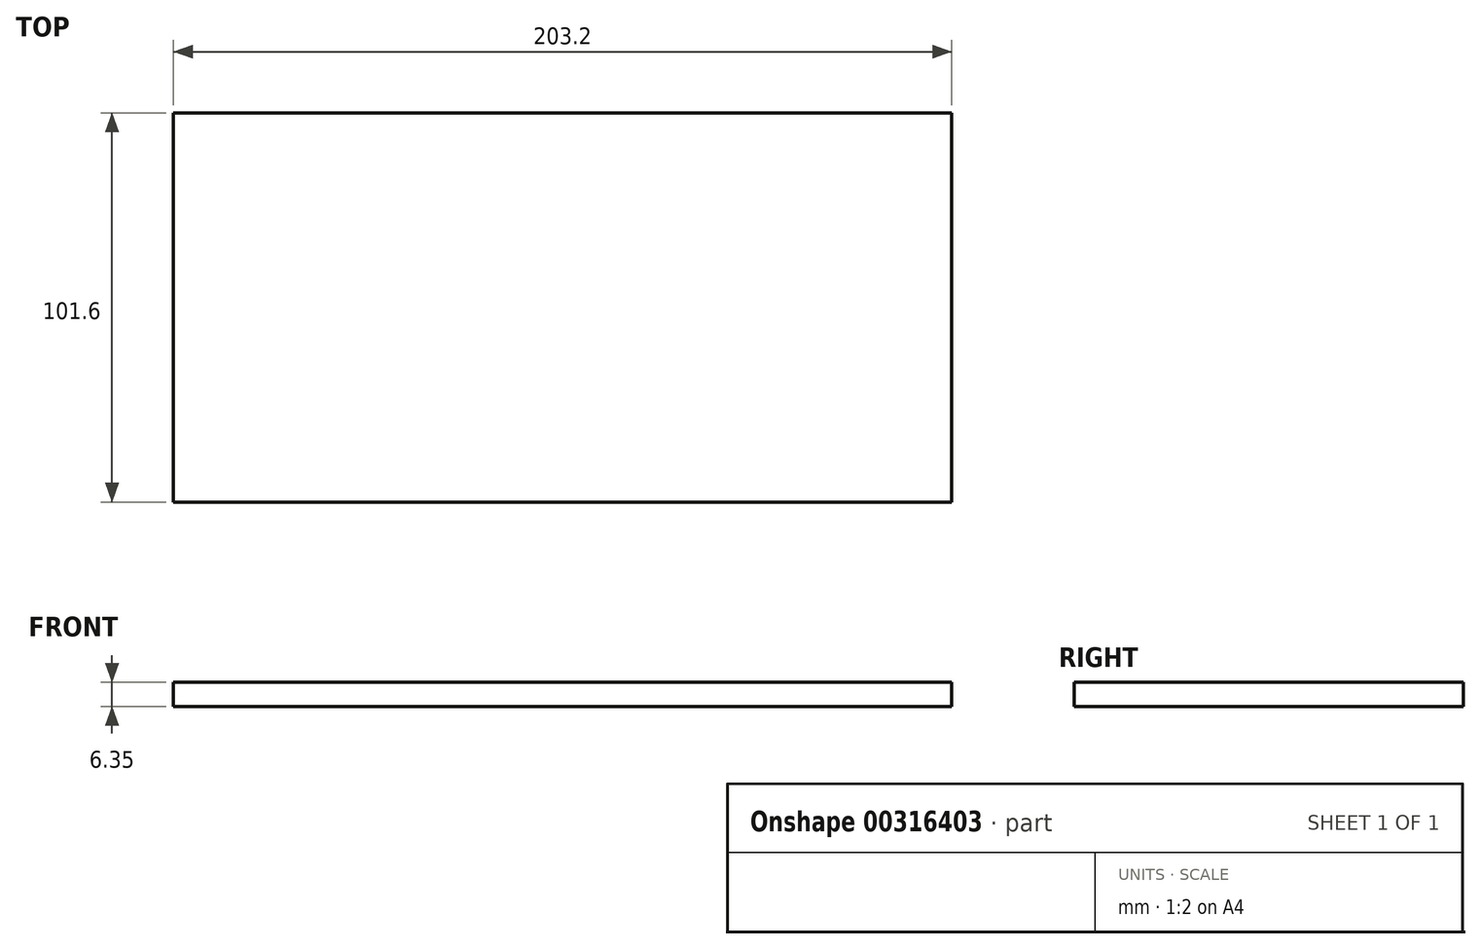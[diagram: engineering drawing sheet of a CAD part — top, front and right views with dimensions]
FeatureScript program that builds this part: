
annotation { "Feature Type Name" : "Feature", "Feature Type Description" : "" }
export const myFeature = defineFeature(function(context is Context, id is Id, definition is map)
    precondition{}
    {
        {
            var Q0;
            Q0=qCreatedBy(makeId("Top.planeOp"),FACE);
            var sketch = newSketch(context, id + "F0", { "sketchPlane" : qUnion([Q0])});
            skLineSegment(sketch, "E0.bottom", {"start": v(0, 0) * mm, "end": v(203.2, 0) * mm});
            skLineSegment(sketch, "E0.top", {"start": v(0, 101.6) * mm, "end": v(203.2, 101.6) * mm});
            skLineSegment(sketch, "E0.left", {"start": v(0, 0) * mm, "end": v(0, 101.6) * mm});
            skLineSegment(sketch, "E0.right", {"start": v(203.2, 0) * mm, "end": v(203.2, 101.6) * mm});
            skSolve(sketch);
        }
        {
            var Q0;
            Q0=makeQuery(id+"F0.imprint","IMPRINT",FACE,{"disambiguationData":[TD([[makeQuery(id+"F0.imprint","IMPRINT",EDGE,{"derivedFrom":sQuery(id+"F0.wireOp",EDGE,"E0.bottom")}),1.0]])]});
            extrude(context, id + "F1", {"entities" : qUnion([Q0]), "depth" : 6.35 * mm});
        }
    });
